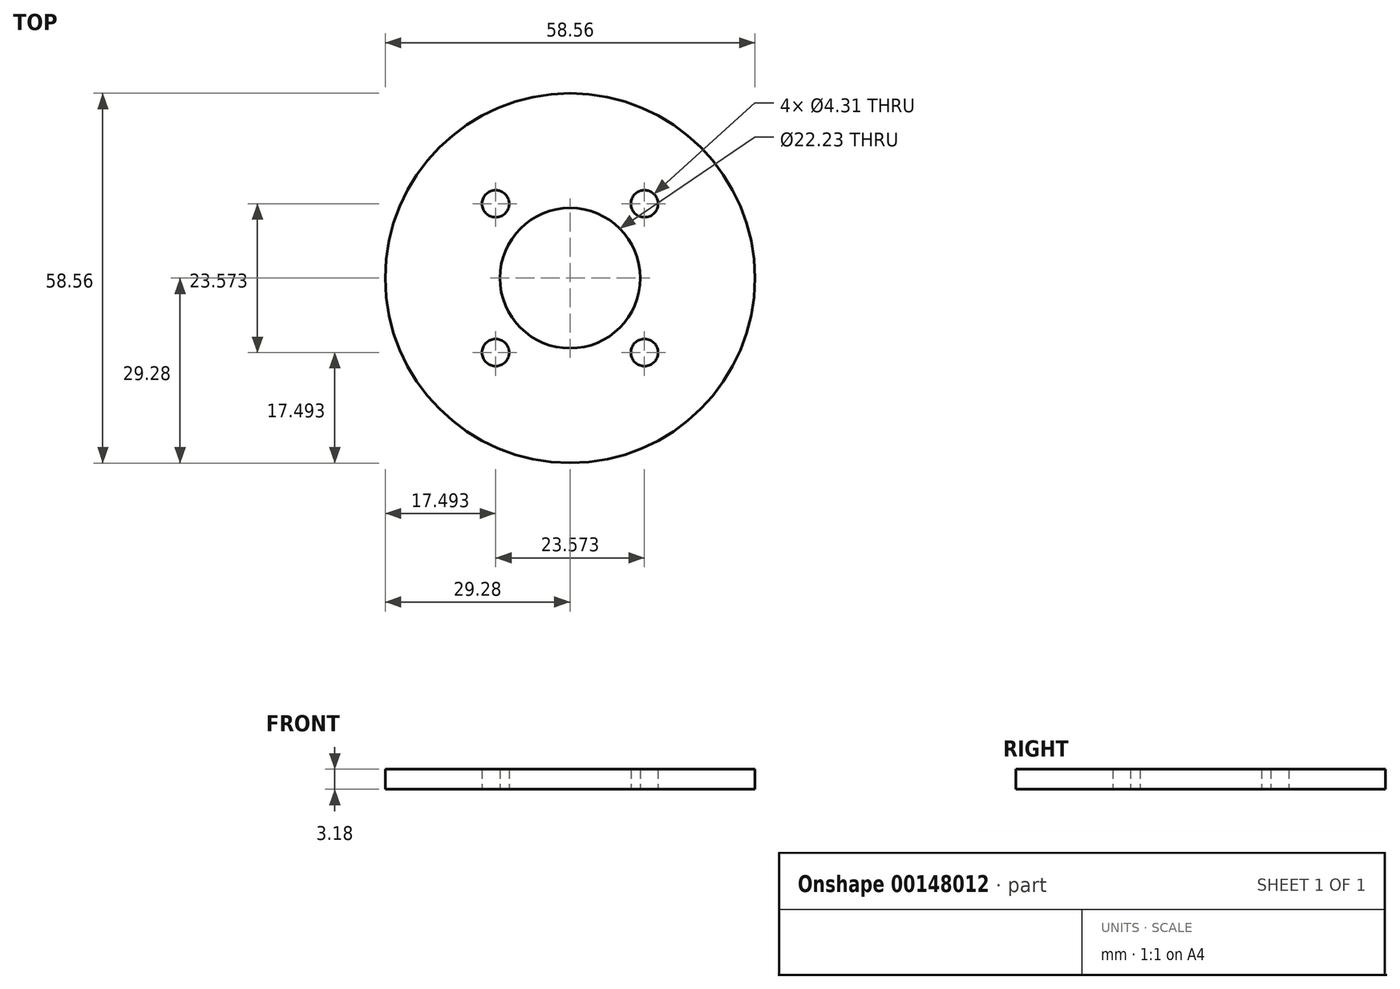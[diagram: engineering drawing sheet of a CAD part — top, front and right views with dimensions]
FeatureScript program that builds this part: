
annotation { "Feature Type Name" : "Feature", "Feature Type Description" : "" }
export const myFeature = defineFeature(function(context is Context, id is Id, definition is map)
    precondition{}
    {
        {
            var Q0;
            Q0=qCreatedBy(makeId("Top.planeOp"),FACE);
            var sketch = newSketch(context, id + "F0", { "sketchPlane" : qUnion([Q0])});
            skCircle(sketch, "E0", {"center": v(0, 0) * mm, "radius": 29.28 * mm});
            skCircle(sketch, "E1", {"center": v(0, 0) * mm, "radius": 11.11 * mm});
            skLineSegment(sketch, "E2.bottom", {"start": v(-11.79, 11.79) * mm, "end": v(11.79, 11.79) * mm, "construction": true});
            skLineSegment(sketch, "E2.top", {"start": v(-11.79, -11.79) * mm, "end": v(11.79, -11.79) * mm, "construction": true});
            skLineSegment(sketch, "E2.left", {"start": v(-11.79, 11.79) * mm, "end": v(-11.79, -11.79) * mm, "construction": true});
            skLineSegment(sketch, "E2.right", {"start": v(11.79, 11.79) * mm, "end": v(11.79, -11.79) * mm, "construction": true});
            skCircle(sketch, "E3", {"center": v(11.79, 11.79) * mm, "radius": 2.15 * mm});
            skCircle(sketch, "E4", {"center": v(-11.79, 11.79) * mm, "radius": 2.15 * mm});
            skCircle(sketch, "E5", {"center": v(-11.79, -11.79) * mm, "radius": 2.15 * mm});
            skCircle(sketch, "E6", {"center": v(11.79, -11.79) * mm, "radius": 2.15 * mm});
            skCircle(sketch, "E7", {"center": v(-11.79, -11.79) * mm, "radius": 3.97 * mm, "construction": true});
            skCircle(sketch, "E8", {"center": v(11.79, 11.79) * mm, "radius": 3.97 * mm, "construction": true});
            skSolve(sketch);
        }
        {
            var Q0;
            Q0=qSketchRegion(id+"F0",true);
            extrude(context, id + "F1", {"entities" : qUnion([Q0]), "depth" : 3.17 * mm});
        }
    });
